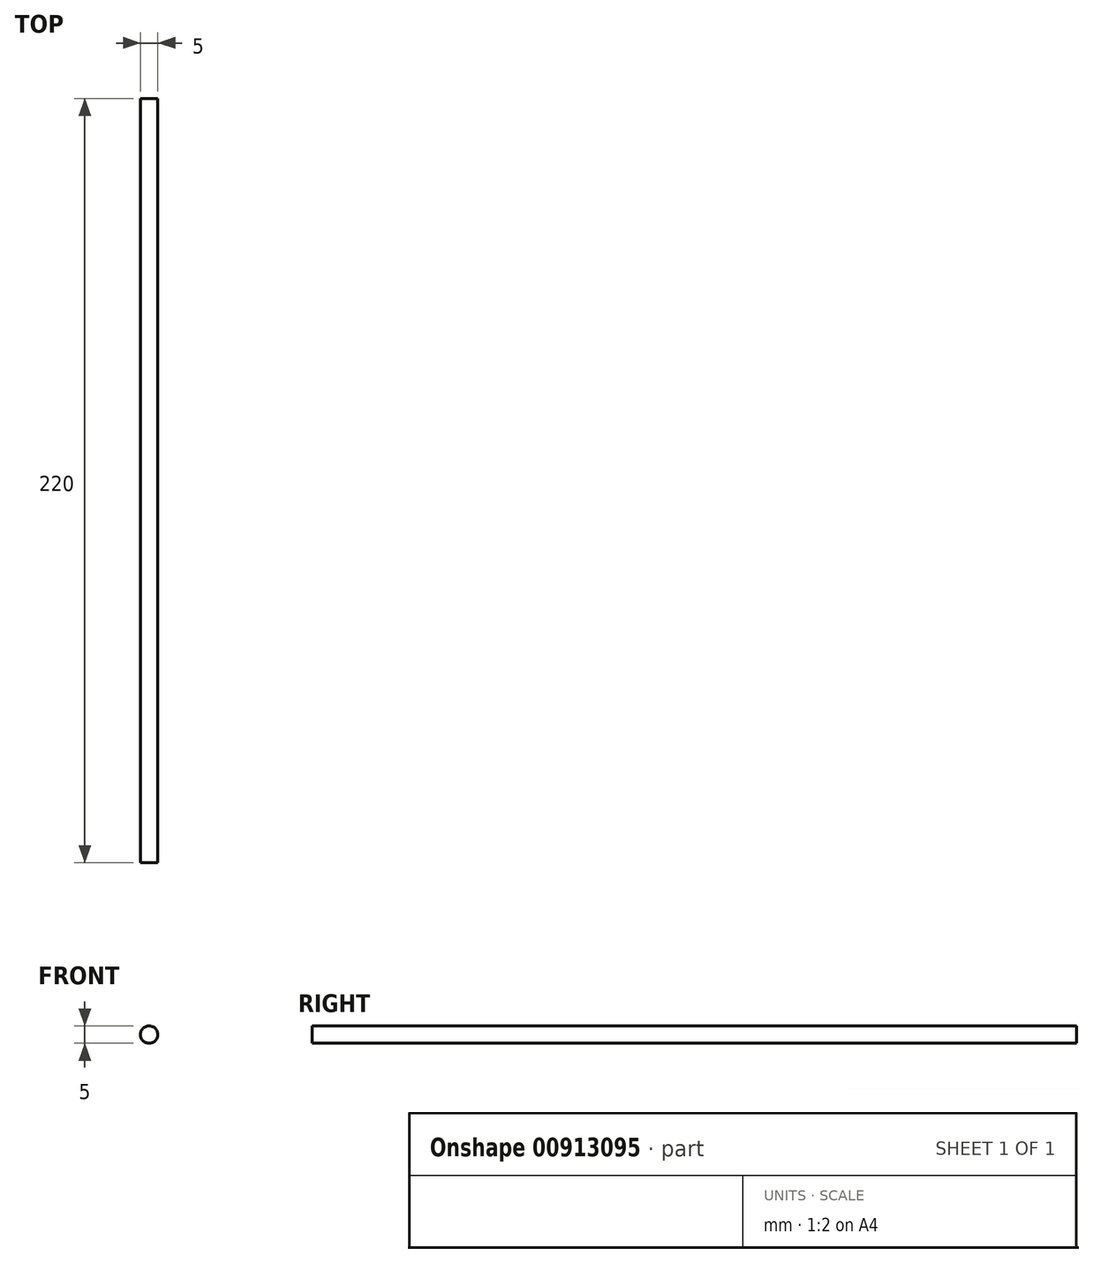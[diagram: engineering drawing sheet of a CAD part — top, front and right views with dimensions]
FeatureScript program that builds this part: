
annotation { "Feature Type Name" : "Feature", "Feature Type Description" : "" }
export const myFeature = defineFeature(function(context is Context, id is Id, definition is map)
    precondition{}
    {
        {
            var Q0;
            Q0=qCreatedBy(makeId("Front.planeOp"),FACE);
            var sketch = newSketch(context, id + "F0", { "sketchPlane" : qUnion([Q0])});
            skCircle(sketch, "E0", {"center": v(0, 0) * mm, "radius": 2.5 * mm});
            skSolve(sketch);
        }
        {
            var Q0;
            Q0 = qSketchRegion(id + "F0", true);
            extrude(context, id + "F1", {"entities" : qUnion([Q0]), "depth" : 220 * mm, "offsetDistance" : 25 * mm});
        }
    });
